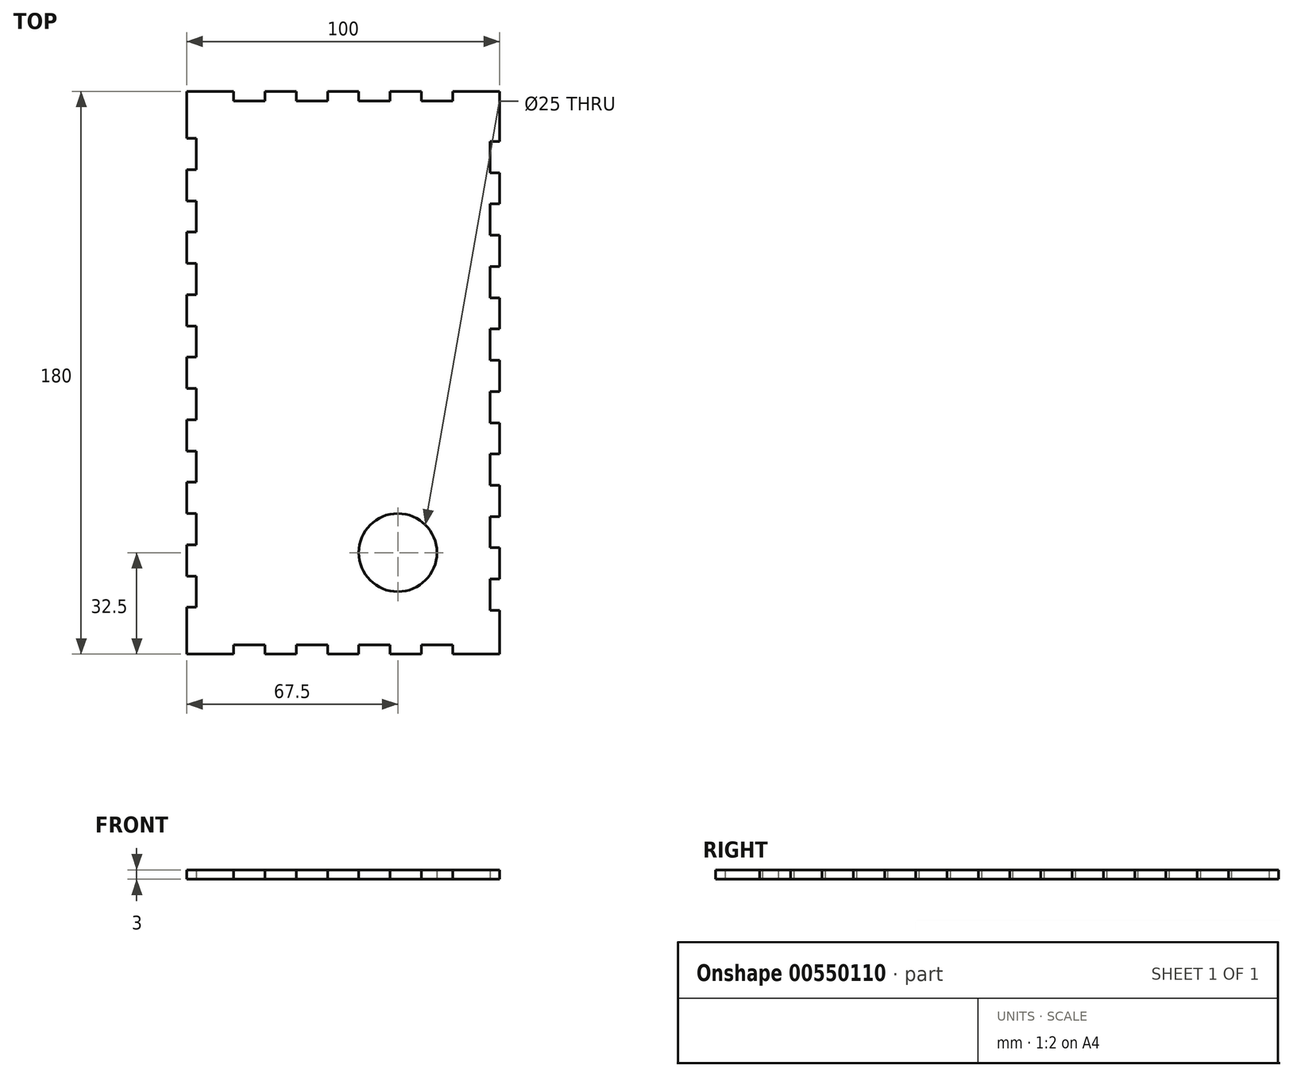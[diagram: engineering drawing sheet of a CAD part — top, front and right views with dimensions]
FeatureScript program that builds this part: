
annotation { "Feature Type Name" : "Feature", "Feature Type Description" : "" }
export const myFeature = defineFeature(function(context is Context, id is Id, definition is map)
    precondition{}
    {
        {
            var Q0;
            Q0=qCreatedBy(makeId("Top.planeOp"),FACE);
            var sketch = newSketch(context, id + "F0", { "sketchPlane" : qUnion([Q0])});
            skPoint(sketch, "E0", {"position": v(0, 0) * mm});
            skCircle(sketch, "E1", {"center": v(20.5, -57.5) * mm, "radius": 12.5 * mm});
            skLineSegment(sketch, "E2", {"start": v(-47, -5) * mm, "end": v(-44, -5) * mm});
            skLineSegment(sketch, "E3", {"start": v(-44, -5) * mm, "end": v(-44, -15) * mm});
            skLineSegment(sketch, "E4", {"start": v(-44, -15) * mm, "end": v(-47, -15) * mm});
            skLineSegment(sketch, "E5", {"start": v(-47, -15) * mm, "end": v(-47, -25) * mm});
            skLineSegment(sketch, "E6", {"start": v(-47, -25) * mm, "end": v(-44, -25) * mm});
            skLineSegment(sketch, "E7", {"start": v(-44, -25) * mm, "end": v(-44, -35) * mm});
            skLineSegment(sketch, "E8", {"start": v(-44, -35) * mm, "end": v(-47, -35) * mm});
            skLineSegment(sketch, "E9", {"start": v(-47, -35) * mm, "end": v(-47, -45) * mm});
            skLineSegment(sketch, "E10", {"start": v(-47, -45) * mm, "end": v(-44, -45) * mm});
            skLineSegment(sketch, "E11", {"start": v(-44, -45) * mm, "end": v(-44, -55) * mm});
            skLineSegment(sketch, "E12", {"start": v(-44, -55) * mm, "end": v(-47, -55) * mm});
            skLineSegment(sketch, "E13", {"start": v(-47, -55) * mm, "end": v(-47, -65) * mm});
            skLineSegment(sketch, "E14", {"start": v(-47, -65) * mm, "end": v(-44, -65) * mm});
            skLineSegment(sketch, "E15", {"start": v(-44, -65) * mm, "end": v(-44, -75) * mm});
            skLineSegment(sketch, "E16", {"start": v(-44, -75) * mm, "end": v(-47, -75) * mm});
            skLineSegment(sketch, "E17", {"start": v(-47, -75) * mm, "end": v(-47, -90) * mm});
            skLineSegment(sketch, "E18", {"start": v(-47, -5) * mm, "end": v(-47, 0) * mm});
            skLineSegment(sketch, "E19.MirrorCS", {"start": v(-44, 35) * mm, "end": v(-47, 35) * mm});
            skLineSegment(sketch, "E20.MirrorCS", {"start": v(-44, 55) * mm, "end": v(-47, 55) * mm});
            skLineSegment(sketch, "E21.MirrorCS", {"start": v(-44, 15) * mm, "end": v(-47, 15) * mm});
            skLineSegment(sketch, "E22.MirrorCS", {"start": v(-47, 5) * mm, "end": v(-44, 5) * mm});
            skLineSegment(sketch, "E23.MirrorCS", {"start": v(-44, 75) * mm, "end": v(-47, 75) * mm});
            skLineSegment(sketch, "E24.MirrorCS", {"start": v(-47, 45) * mm, "end": v(-44, 45) * mm});
            skLineSegment(sketch, "E25.MirrorCS", {"start": v(-47, 25) * mm, "end": v(-44, 25) * mm});
            skLineSegment(sketch, "E26.MirrorCS", {"start": v(-47, 65) * mm, "end": v(-44, 65) * mm});
            skLineSegment(sketch, "E27.MirrorCS", {"start": v(-44, 25) * mm, "end": v(-44, 35) * mm});
            skLineSegment(sketch, "E28.MirrorCS", {"start": v(-47, 55) * mm, "end": v(-47, 65) * mm});
            skLineSegment(sketch, "E29.MirrorCS", {"start": v(-47, 35) * mm, "end": v(-47, 45) * mm});
            skLineSegment(sketch, "E30.MirrorCS", {"start": v(-47, 15) * mm, "end": v(-47, 25) * mm});
            skLineSegment(sketch, "E31.MirrorCS", {"start": v(-47, 5) * mm, "end": v(-47, 0) * mm});
            skLineSegment(sketch, "E32.MirrorCS", {"start": v(-44, 65) * mm, "end": v(-44, 75) * mm});
            skLineSegment(sketch, "E33.MirrorCS", {"start": v(-47, 75) * mm, "end": v(-47, 90) * mm});
            skLineSegment(sketch, "E34.MirrorCS", {"start": v(-44, 45) * mm, "end": v(-44, 55) * mm});
            skLineSegment(sketch, "E35.MirrorCS", {"start": v(-44, 5) * mm, "end": v(-44, 15) * mm});
            skLineSegment(sketch, "E36", {"start": v(53, 90) * mm, "end": v(38, 90) * mm});
            skLineSegment(sketch, "E37", {"start": v(38, 90) * mm, "end": v(38, 87) * mm});
            skLineSegment(sketch, "E38", {"start": v(38, 87) * mm, "end": v(28, 87) * mm});
            skLineSegment(sketch, "E39", {"start": v(28, 87) * mm, "end": v(28, 90) * mm});
            skLineSegment(sketch, "E40", {"start": v(28, 90) * mm, "end": v(18, 90) * mm});
            skLineSegment(sketch, "E41", {"start": v(18, 90) * mm, "end": v(18, 87) * mm});
            skLineSegment(sketch, "E42", {"start": v(18, 87) * mm, "end": v(8, 87) * mm});
            skLineSegment(sketch, "E43", {"start": v(8, 87) * mm, "end": v(8, 90) * mm});
            skLineSegment(sketch, "E44", {"start": v(8, 90) * mm, "end": v(-2, 90) * mm});
            skLineSegment(sketch, "E45", {"start": v(-2, 90) * mm, "end": v(-2, 87) * mm});
            skLineSegment(sketch, "E46", {"start": v(-2, 87) * mm, "end": v(-12, 87) * mm});
            skLineSegment(sketch, "E47", {"start": v(-12, 87) * mm, "end": v(-12, 90) * mm});
            skLineSegment(sketch, "E48", {"start": v(-12, 90) * mm, "end": v(-22, 90) * mm});
            skLineSegment(sketch, "E49", {"start": v(-22, 90) * mm, "end": v(-22, 87) * mm});
            skLineSegment(sketch, "E50", {"start": v(-22, 87) * mm, "end": v(-32, 87) * mm});
            skLineSegment(sketch, "E51", {"start": v(-32, 87) * mm, "end": v(-32, 90) * mm});
            skLineSegment(sketch, "E52", {"start": v(-32, 90) * mm, "end": v(-47, 90) * mm});
            skLineSegment(sketch, "E53", {"start": v(-47, -90) * mm, "end": v(-32, -90) * mm});
            skLineSegment(sketch, "E54", {"start": v(-32, -90) * mm, "end": v(-32, -87) * mm});
            skLineSegment(sketch, "E55", {"start": v(-32, -87) * mm, "end": v(-22, -87) * mm});
            skLineSegment(sketch, "E56", {"start": v(-22, -87) * mm, "end": v(-22, -90) * mm});
            skLineSegment(sketch, "E57", {"start": v(-22, -90) * mm, "end": v(-12, -90) * mm});
            skLineSegment(sketch, "E58", {"start": v(-12, -90) * mm, "end": v(-12, -87) * mm});
            skLineSegment(sketch, "E59", {"start": v(-12, -87) * mm, "end": v(-2, -87) * mm});
            skLineSegment(sketch, "E60", {"start": v(-2, -87) * mm, "end": v(-2, -90) * mm});
            skLineSegment(sketch, "E61", {"start": v(-2, -90) * mm, "end": v(8, -90) * mm});
            skLineSegment(sketch, "E62", {"start": v(8, -90) * mm, "end": v(8, -87) * mm});
            skLineSegment(sketch, "E63", {"start": v(8, -87) * mm, "end": v(18, -87) * mm});
            skLineSegment(sketch, "E64", {"start": v(18, -87) * mm, "end": v(18, -90) * mm});
            skLineSegment(sketch, "E65", {"start": v(18, -90) * mm, "end": v(28, -90) * mm});
            skLineSegment(sketch, "E66", {"start": v(28, -90) * mm, "end": v(28, -87) * mm});
            skLineSegment(sketch, "E67", {"start": v(28, -87) * mm, "end": v(38, -87) * mm});
            skLineSegment(sketch, "E68", {"start": v(38, -87) * mm, "end": v(38, -90) * mm});
            skLineSegment(sketch, "E69", {"start": v(38, -90) * mm, "end": v(53, -90) * mm});
            skLineSegment(sketch, "E70", {"start": v(53, 4.03) * mm, "end": v(50, 4.03) * mm});
            skLineSegment(sketch, "E71", {"start": v(50, 4.03) * mm, "end": v(50, 14.03) * mm});
            skLineSegment(sketch, "E72", {"start": v(50, 14.03) * mm, "end": v(53, 14.03) * mm});
            skLineSegment(sketch, "E73", {"start": v(53, 14.03) * mm, "end": v(53, 24.03) * mm});
            skLineSegment(sketch, "E74", {"start": v(53, 24.03) * mm, "end": v(50, 24.03) * mm});
            skLineSegment(sketch, "E75", {"start": v(50, 24.03) * mm, "end": v(50, 34.03) * mm});
            skLineSegment(sketch, "E76", {"start": v(50, 34.03) * mm, "end": v(53, 34.03) * mm});
            skLineSegment(sketch, "E77", {"start": v(53, 34.03) * mm, "end": v(53, 44.03) * mm});
            skLineSegment(sketch, "E78", {"start": v(53, 44.03) * mm, "end": v(50, 44.03) * mm});
            skLineSegment(sketch, "E79", {"start": v(50, 44.03) * mm, "end": v(50, 54.03) * mm});
            skLineSegment(sketch, "E80", {"start": v(50, 54.03) * mm, "end": v(53, 54.03) * mm});
            skLineSegment(sketch, "E81", {"start": v(53, 54.03) * mm, "end": v(53, 64.03) * mm});
            skLineSegment(sketch, "E82", {"start": v(53, 64.03) * mm, "end": v(50, 64.03) * mm});
            skLineSegment(sketch, "E83", {"start": v(50, 64.03) * mm, "end": v(50, 74.03) * mm});
            skLineSegment(sketch, "E84", {"start": v(50, 74.03) * mm, "end": v(53, 74.03) * mm});
            skLineSegment(sketch, "E85", {"start": v(53, 74.03) * mm, "end": v(53, 90) * mm});
            skLineSegment(sketch, "E86", {"start": v(53, 4.03) * mm, "end": v(53, 0) * mm});
            skLineSegment(sketch, "E87.MirrorCS", {"start": v(50, -35.97) * mm, "end": v(53, -35.97) * mm});
            skLineSegment(sketch, "E88.MirrorCS", {"start": v(50, -55.97) * mm, "end": v(53, -55.97) * mm});
            skLineSegment(sketch, "E89.MirrorCS", {"start": v(50, -15.97) * mm, "end": v(53, -15.97) * mm});
            skLineSegment(sketch, "E90.MirrorCS", {"start": v(53, -5.97) * mm, "end": v(50, -5.97) * mm});
            skLineSegment(sketch, "E91.MirrorCS", {"start": v(50, -75.97) * mm, "end": v(53, -75.97) * mm});
            skLineSegment(sketch, "E92.MirrorCS", {"start": v(53, -45.97) * mm, "end": v(50, -45.97) * mm});
            skLineSegment(sketch, "E93.MirrorCS", {"start": v(53, -25.97) * mm, "end": v(50, -25.97) * mm});
            skLineSegment(sketch, "E94.MirrorCS", {"start": v(53, -65.97) * mm, "end": v(50, -65.97) * mm});
            skLineSegment(sketch, "E95.MirrorCS", {"start": v(50, -25.97) * mm, "end": v(50, -35.97) * mm});
            skLineSegment(sketch, "E96.MirrorCS", {"start": v(53, -55.97) * mm, "end": v(53, -65.97) * mm});
            skLineSegment(sketch, "E97.MirrorCS", {"start": v(53, -35.97) * mm, "end": v(53, -45.97) * mm});
            skLineSegment(sketch, "E98.MirrorCS", {"start": v(53, -15.97) * mm, "end": v(53, -25.97) * mm});
            skLineSegment(sketch, "E99.MirrorCS", {"start": v(53, -5.97) * mm, "end": v(53, 0) * mm});
            skLineSegment(sketch, "E100.MirrorCS", {"start": v(50, -65.97) * mm, "end": v(50, -75.97) * mm});
            skLineSegment(sketch, "E101.MirrorCS", {"start": v(53, -75.97) * mm, "end": v(53, -90) * mm});
            skLineSegment(sketch, "E102.MirrorCS", {"start": v(50, -45.97) * mm, "end": v(50, -55.97) * mm});
            skLineSegment(sketch, "E103.MirrorCS", {"start": v(50, -5.97) * mm, "end": v(50, -15.97) * mm});
            skSolve(sketch);
        }
        {
            var Q0;
            Q0 = qSketchRegion(id + "F0", true);
            extrude(context, id + "F1", {"entities" : qUnion([Q0]), "depth" : 3 * mm, "offsetDistance" : 25 * mm, "symmetric" : true});
        }
    });
